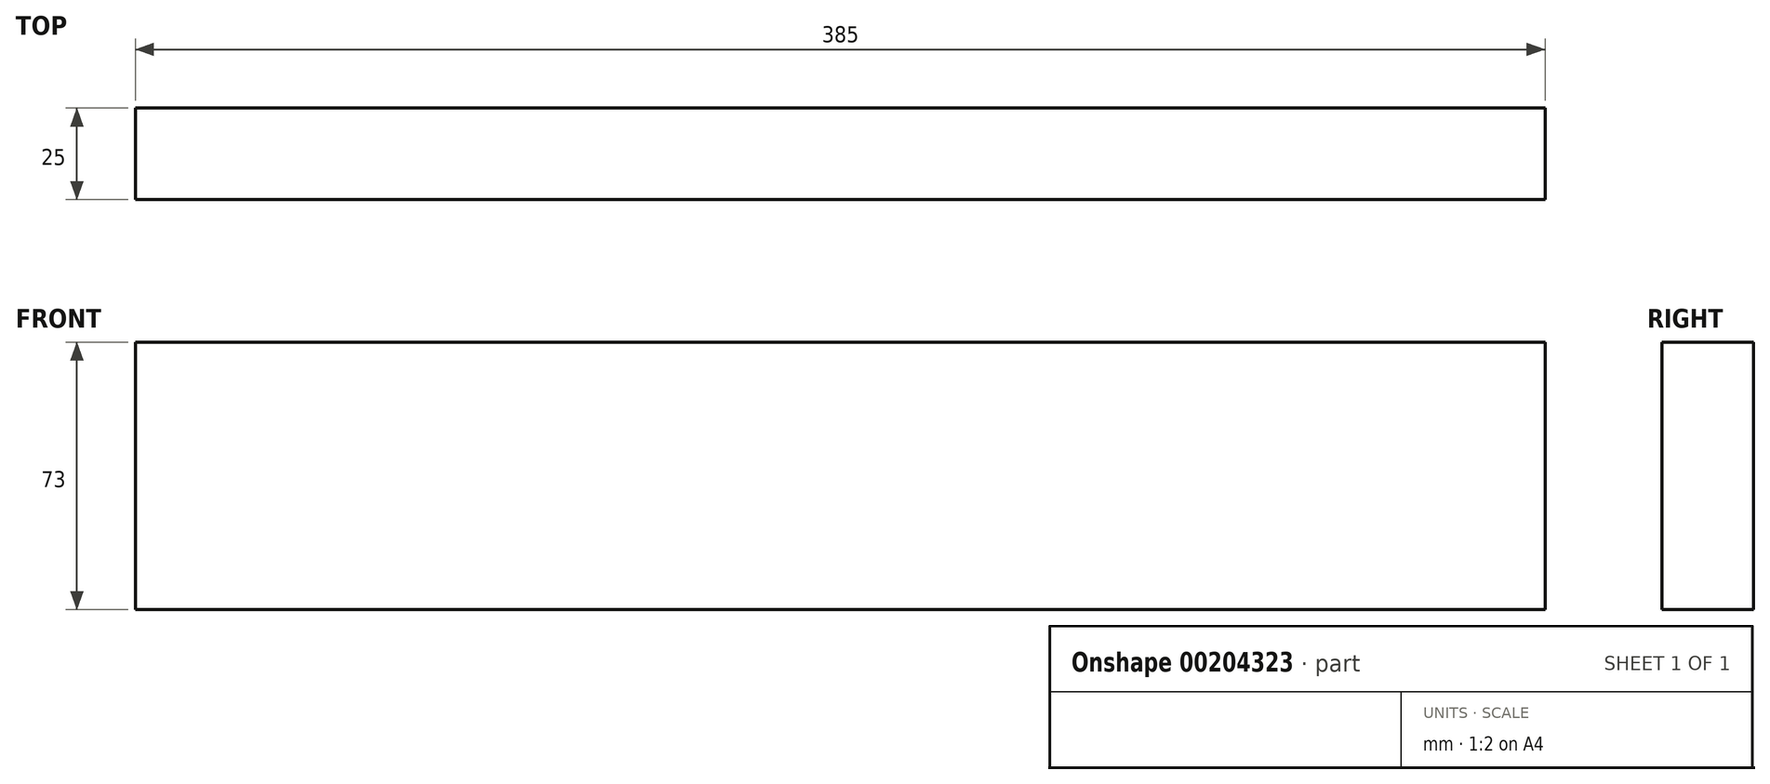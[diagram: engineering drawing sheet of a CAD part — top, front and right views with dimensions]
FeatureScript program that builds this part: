
annotation { "Feature Type Name" : "Feature", "Feature Type Description" : "" }
export const myFeature = defineFeature(function(context is Context, id is Id, definition is map)
    precondition{}
    {
        {
            var Q0;
            Q0=qCreatedBy(makeId("Front.planeOp"),FACE);
            var sketch = newSketch(context, id + "F0", { "sketchPlane" : qUnion([Q0])});
            skLineSegment(sketch, "E0.bottom", {"start": v(0, 0) * mm, "end": v(385, 0) * mm});
            skLineSegment(sketch, "E0.top", {"start": v(0, 73) * mm, "end": v(385, 73) * mm});
            skLineSegment(sketch, "E0.left", {"start": v(0, 0) * mm, "end": v(0, 73) * mm});
            skLineSegment(sketch, "E0.right", {"start": v(385, 0) * mm, "end": v(385, 73) * mm});
            skSolve(sketch);
        }
        {
            var Q0;
            Q0=makeQuery(id+"F0.imprint","IMPRINT",FACE,{"disambiguationData":[TD([[makeQuery(id+"F0.imprint","IMPRINT",EDGE,{"derivedFrom":sQuery(id+"F0.wireOp",EDGE,"E0.bottom")}),1.0]])]});
            extrude(context, id + "F1", {"entities" : qUnion([Q0]), "depth" : 25 * mm});
        }
    });
